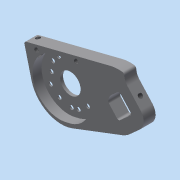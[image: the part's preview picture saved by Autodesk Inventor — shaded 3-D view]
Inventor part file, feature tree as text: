
AUTODESK INVENTOR PART (.ipt)
format: ipt  version: 2014 SP1 (Build 180222100, 222)  size: 296,960 bytes
history: native  units: in
note: dims shown in document units (in); Inventor stores cm internally (conversion verified against a paired STEP export)
features: sketch x10, other x3
ambient origin geometry x8: Origin, YZ Plane, XZ Plane, XY Plane, X Axis, Y Axis, Z Axis, Center Point
bodies: Solid1 (feature_tree)
feature tree (13):
  other  "mount_alt.ipt"
  other  "Solid3::mount_alt.ipt"
  other  "TaggingFeature1"
  sketch  "Sketch1"  dims[d0=0.3937in]
  sketch  "Sketch17"
  sketch  "Sketch12"  dims[d91=0.5in d92=0.0in d93=1.0in d94=0.1in d95=0.5in d99=0.19in d100=0.19in d101=0.355in d102=0.25in d105=1.0in d106=0.0in d107=1.0in d108=0.0in d120=0.375in d121=0.0in d122=0.25in d123=0.2in d124=0.0938in d127=0.1in d136=0.5in d137=0.0in d138=0.19in d140=0.15in d146=2.5063in d147=0.9398in d148=2.2047in d149=0.19in d150=0.19in d154=0.0in d161=0.0866in d167=0.25in d178=2.2835in d179=2.2835in d181=0.5in d182=0.1875in d184=0.1875in d185=1.72in d192=0.19in d193=0.15in d194=0.15in d195=1.0in d196=0.0in d117=3.9751in d118=2.5984in d125=2.5984in d126=4.7534in d128=2.5984in d129=4.7983in]
  sketch  "Sketch13"  dims[d2=0.8661in d3=0.1693in d5=0.8661in d6=2.5984in d7=2.4577in d13=1.5748in d17=2.454in d18=1.9042in]
  sketch  "Sketch16"  dims[d15=360.0deg]
  sketch  "Sketch18"
  sketch  "Sketch19"
  sketch  "Sketch21"
  sketch  "Sketch22"
  sketch  "Sketch26"
